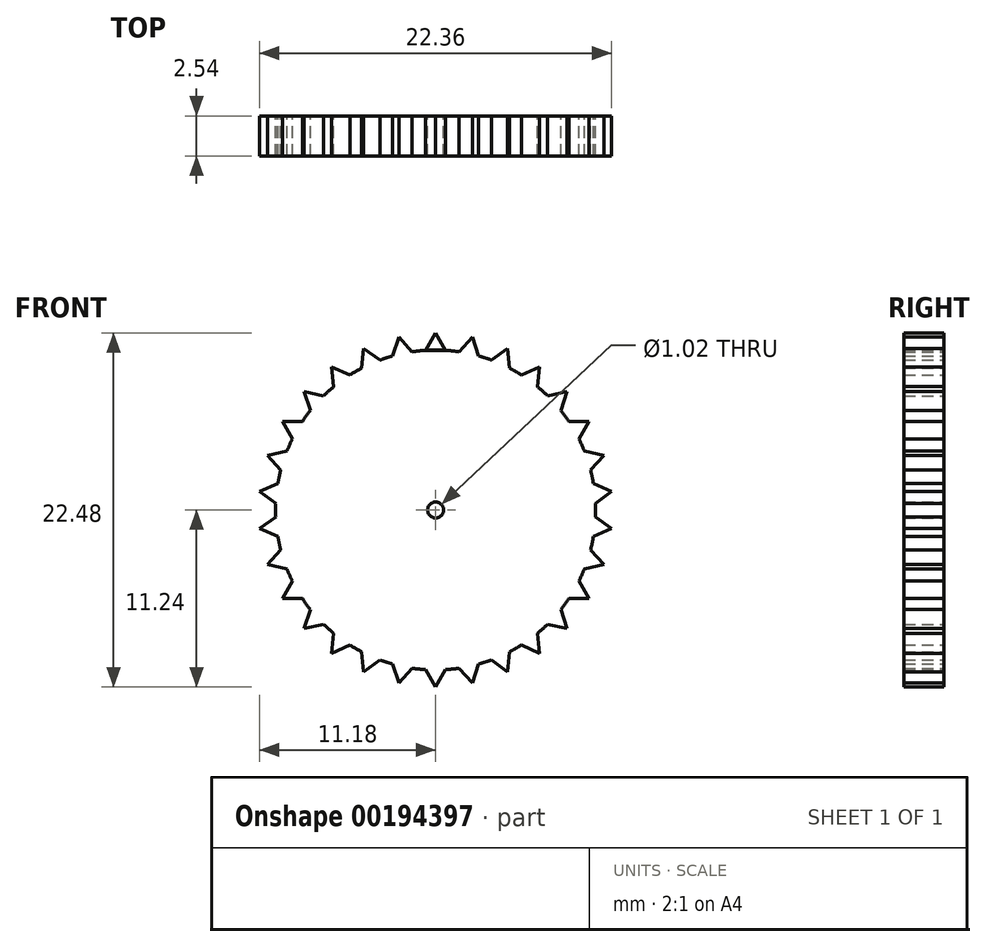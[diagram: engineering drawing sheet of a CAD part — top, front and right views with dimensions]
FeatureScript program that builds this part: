
annotation { "Feature Type Name" : "Feature", "Feature Type Description" : "" }
export const myFeature = defineFeature(function(context is Context, id is Id, definition is map)
    precondition{}
    {
        {
            var Q0;
            Q0=qCreatedBy(makeId("Front.planeOp"),FACE);
            var sketch = newSketch(context, id + "F0", { "sketchPlane" : qUnion([Q0])});
            skCircle(sketch, "E0", {"center": v(0, 0) * mm, "radius": 10.16 * mm});
            skCircle(sketch, "E1", {"center": v(0, 0) * mm, "radius": 0.5 * mm});
            skLineSegment(sketch, "E2", {"start": v(0, 11.24) * mm, "end": v(-0.64, 10.14) * mm});
            skLineSegment(sketch, "E3", {"start": v(-0.64, 10.14) * mm, "end": v(0.64, 10.14) * mm});
            skLineSegment(sketch, "E4", {"start": v(0.64, 10.14) * mm, "end": v(0, 11.24) * mm});
            skLineSegment(sketch, "E5.1.0", {"start": v(-1.49, 10.05) * mm, "end": v(-2.34, 11) * mm});
            skLineSegment(sketch, "E5.1.1", {"start": v(-2.34, 11) * mm, "end": v(-2.73, 9.79) * mm});
            skLineSegment(sketch, "E5.2.0", {"start": v(-3.54, 9.52) * mm, "end": v(-4.57, 10.27) * mm});
            skLineSegment(sketch, "E5.2.1", {"start": v(-4.57, 10.27) * mm, "end": v(-4.7, 9) * mm});
            skLineSegment(sketch, "E5.3.0", {"start": v(-5.45, 8.58) * mm, "end": v(-6.6, 9.1) * mm});
            skLineSegment(sketch, "E5.3.1", {"start": v(-6.6, 9.1) * mm, "end": v(-6.47, 7.83) * mm});
            skLineSegment(sketch, "E5.4.0", {"start": v(-7.11, 7.26) * mm, "end": v(-8.35, 7.52) * mm});
            skLineSegment(sketch, "E5.4.1", {"start": v(-8.35, 7.52) * mm, "end": v(-7.96, 6.31) * mm});
            skLineSegment(sketch, "E5.5.0", {"start": v(-8.46, 5.62) * mm, "end": v(-9.73, 5.62) * mm});
            skLineSegment(sketch, "E5.5.1", {"start": v(-9.73, 5.62) * mm, "end": v(-9.1, 4.52) * mm});
            skLineSegment(sketch, "E5.6.0", {"start": v(-9.45, 3.74) * mm, "end": v(-10.7, 3.47) * mm});
            skLineSegment(sketch, "E5.6.1", {"start": v(-10.7, 3.47) * mm, "end": v(-9.84, 2.53) * mm});
            skLineSegment(sketch, "E5.7.0", {"start": v(-10.02, 1.7) * mm, "end": v(-11.18, 1.17) * mm});
            skLineSegment(sketch, "E5.7.1", {"start": v(-11.18, 1.17) * mm, "end": v(-10.15, 0.43) * mm});
            skLineSegment(sketch, "E5.8.0", {"start": v(-10.15, -0.43) * mm, "end": v(-11.18, -1.17) * mm});
            skLineSegment(sketch, "E5.8.1", {"start": v(-11.18, -1.17) * mm, "end": v(-10.02, -1.7) * mm});
            skLineSegment(sketch, "E5.9.0", {"start": v(-9.84, -2.53) * mm, "end": v(-10.7, -3.47) * mm});
            skLineSegment(sketch, "E5.9.1", {"start": v(-10.7, -3.47) * mm, "end": v(-9.45, -3.74) * mm});
            skLineSegment(sketch, "E5.10.0", {"start": v(-9.1, -4.52) * mm, "end": v(-9.73, -5.62) * mm});
            skLineSegment(sketch, "E5.10.1", {"start": v(-9.73, -5.62) * mm, "end": v(-8.46, -5.62) * mm});
            skLineSegment(sketch, "E5.11.0", {"start": v(-7.96, -6.31) * mm, "end": v(-8.35, -7.52) * mm});
            skLineSegment(sketch, "E5.11.1", {"start": v(-8.35, -7.52) * mm, "end": v(-7.11, -7.26) * mm});
            skLineSegment(sketch, "E5.12.0", {"start": v(-6.47, -7.83) * mm, "end": v(-6.6, -9.1) * mm});
            skLineSegment(sketch, "E5.12.1", {"start": v(-6.6, -9.1) * mm, "end": v(-5.45, -8.58) * mm});
            skLineSegment(sketch, "E5.13.0", {"start": v(-4.7, -9) * mm, "end": v(-4.57, -10.27) * mm});
            skLineSegment(sketch, "E5.13.1", {"start": v(-4.57, -10.27) * mm, "end": v(-3.54, -9.52) * mm});
            skLineSegment(sketch, "E5.14.0", {"start": v(-2.73, -9.79) * mm, "end": v(-2.34, -11) * mm});
            skLineSegment(sketch, "E5.14.1", {"start": v(-2.34, -11) * mm, "end": v(-1.49, -10.05) * mm});
            skLineSegment(sketch, "E5.15.0", {"start": v(-0.64, -10.14) * mm, "end": v(0, -11.24) * mm});
            skLineSegment(sketch, "E5.15.1", {"start": v(0, -11.24) * mm, "end": v(0.64, -10.14) * mm});
            skLineSegment(sketch, "E5.16.0", {"start": v(1.49, -10.05) * mm, "end": v(2.34, -11) * mm});
            skLineSegment(sketch, "E5.16.1", {"start": v(2.34, -11) * mm, "end": v(2.73, -9.79) * mm});
            skLineSegment(sketch, "E5.17.0", {"start": v(3.54, -9.52) * mm, "end": v(4.57, -10.27) * mm});
            skLineSegment(sketch, "E5.17.1", {"start": v(4.57, -10.27) * mm, "end": v(4.7, -9) * mm});
            skLineSegment(sketch, "E5.18.0", {"start": v(5.45, -8.58) * mm, "end": v(6.6, -9.1) * mm});
            skLineSegment(sketch, "E5.18.1", {"start": v(6.6, -9.1) * mm, "end": v(6.47, -7.83) * mm});
            skLineSegment(sketch, "E5.19.0", {"start": v(7.11, -7.26) * mm, "end": v(8.35, -7.52) * mm});
            skLineSegment(sketch, "E5.19.1", {"start": v(8.35, -7.52) * mm, "end": v(7.96, -6.31) * mm});
            skLineSegment(sketch, "E5.20.0", {"start": v(8.46, -5.62) * mm, "end": v(9.73, -5.62) * mm});
            skLineSegment(sketch, "E5.20.1", {"start": v(9.73, -5.62) * mm, "end": v(9.1, -4.52) * mm});
            skLineSegment(sketch, "E5.21.0", {"start": v(9.45, -3.74) * mm, "end": v(10.7, -3.47) * mm});
            skLineSegment(sketch, "E5.21.1", {"start": v(10.7, -3.47) * mm, "end": v(9.84, -2.53) * mm});
            skLineSegment(sketch, "E5.22.0", {"start": v(10.02, -1.7) * mm, "end": v(11.18, -1.17) * mm});
            skLineSegment(sketch, "E5.22.1", {"start": v(11.18, -1.17) * mm, "end": v(10.15, -0.43) * mm});
            skLineSegment(sketch, "E5.23.0", {"start": v(10.15, 0.43) * mm, "end": v(11.18, 1.17) * mm});
            skLineSegment(sketch, "E5.23.1", {"start": v(11.18, 1.17) * mm, "end": v(10.02, 1.7) * mm});
            skLineSegment(sketch, "E5.24.0", {"start": v(9.84, 2.53) * mm, "end": v(10.7, 3.47) * mm});
            skLineSegment(sketch, "E5.24.1", {"start": v(10.7, 3.47) * mm, "end": v(9.45, 3.74) * mm});
            skLineSegment(sketch, "E5.25.0", {"start": v(9.1, 4.52) * mm, "end": v(9.73, 5.62) * mm});
            skLineSegment(sketch, "E5.25.1", {"start": v(9.73, 5.62) * mm, "end": v(8.46, 5.62) * mm});
            skLineSegment(sketch, "E5.26.0", {"start": v(7.96, 6.31) * mm, "end": v(8.35, 7.52) * mm});
            skLineSegment(sketch, "E5.26.1", {"start": v(8.35, 7.52) * mm, "end": v(7.11, 7.26) * mm});
            skLineSegment(sketch, "E5.27.0", {"start": v(6.47, 7.83) * mm, "end": v(6.6, 9.1) * mm});
            skLineSegment(sketch, "E5.27.1", {"start": v(6.6, 9.1) * mm, "end": v(5.45, 8.58) * mm});
            skLineSegment(sketch, "E5.28.0", {"start": v(4.7, 9) * mm, "end": v(4.57, 10.27) * mm});
            skLineSegment(sketch, "E5.28.1", {"start": v(4.57, 10.27) * mm, "end": v(3.54, 9.52) * mm});
            skLineSegment(sketch, "E5.29.0", {"start": v(2.73, 9.79) * mm, "end": v(2.34, 11) * mm});
            skLineSegment(sketch, "E5.29.1", {"start": v(2.34, 11) * mm, "end": v(1.49, 10.05) * mm});
            skSolve(sketch);
        }
        {
            var Q0;
            Q0=makeQuery(id+"F0.imprint","IMPRINT",FACE,{"disambiguationData":[TD([[makeQuery(id+"F0.imprint","IMPRINT",EDGE,{"derivedFrom":sQuery(id+"F0.wireOp",EDGE,"E1")}),-1.0]])]});
            var Q1;
            {var subQ0=sQuery(id+"F0.wireOp",EDGE,"E5.6.0");Q1=makeQuery(id+"F0.imprint","IMPRINT",FACE,{"disambiguationData":[TD([[makeQuery(id+"F0.imprint","IMPRINT",EDGE,{"derivedFrom":subQ0}),1.0]])]});}
            var Q2;
            {var subQ0=sQuery(id+"F0.wireOp",EDGE,"E5.5.0");Q2=makeQuery(id+"F0.imprint","IMPRINT",FACE,{"disambiguationData":[TD([[makeQuery(id+"F0.imprint","IMPRINT",EDGE,{"derivedFrom":subQ0}),1.0]])]});}
            var Q3;
            {var subQ0=sQuery(id+"F0.wireOp",EDGE,"E5.4.0");Q3=makeQuery(id+"F0.imprint","IMPRINT",FACE,{"disambiguationData":[TD([[makeQuery(id+"F0.imprint","IMPRINT",EDGE,{"derivedFrom":subQ0}),1.0]])]});}
            var Q4;
            {var subQ0=sQuery(id+"F0.wireOp",EDGE,"E5.3.0");Q4=makeQuery(id+"F0.imprint","IMPRINT",FACE,{"disambiguationData":[TD([[makeQuery(id+"F0.imprint","IMPRINT",EDGE,{"derivedFrom":subQ0}),1.0]])]});}
            var Q5;
            {var subQ0=sQuery(id+"F0.wireOp",EDGE,"E5.2.0");Q5=makeQuery(id+"F0.imprint","IMPRINT",FACE,{"disambiguationData":[TD([[makeQuery(id+"F0.imprint","IMPRINT",EDGE,{"derivedFrom":subQ0}),1.0]])]});}
            var Q6;
            {var subQ0=sQuery(id+"F0.wireOp",EDGE,"E5.1.0");Q6=makeQuery(id+"F0.imprint","IMPRINT",FACE,{"disambiguationData":[TD([[makeQuery(id+"F0.imprint","IMPRINT",EDGE,{"derivedFrom":subQ0}),1.0]])]});}
            var Q7;
            {var subQ1=sQuery(id+"F0.wireOp",EDGE,"E2");Q7=makeQuery(id+"F0.imprint","IMPRINT",FACE,{"disambiguationData":[TD([[makeQuery(id+"F0.imprint","IMPRINT",EDGE,{"derivedFrom":subQ1}),1.0]])]});}
            var Q8;
            {var subQ0=sQuery(id+"F0.wireOp",EDGE,"E5.29.0");Q8=makeQuery(id+"F0.imprint","IMPRINT",FACE,{"disambiguationData":[TD([[makeQuery(id+"F0.imprint","IMPRINT",EDGE,{"derivedFrom":subQ0}),1.0]])]});}
            var Q9;
            {var subQ0=sQuery(id+"F0.wireOp",EDGE,"E5.28.0");Q9=makeQuery(id+"F0.imprint","IMPRINT",FACE,{"disambiguationData":[TD([[makeQuery(id+"F0.imprint","IMPRINT",EDGE,{"derivedFrom":subQ0}),1.0]])]});}
            var Q10;
            {var subQ0=sQuery(id+"F0.wireOp",EDGE,"E5.27.0");Q10=makeQuery(id+"F0.imprint","IMPRINT",FACE,{"disambiguationData":[TD([[makeQuery(id+"F0.imprint","IMPRINT",EDGE,{"derivedFrom":subQ0}),1.0]])]});}
            var Q11;
            {var subQ0=sQuery(id+"F0.wireOp",EDGE,"E5.26.0");Q11=makeQuery(id+"F0.imprint","IMPRINT",FACE,{"disambiguationData":[TD([[makeQuery(id+"F0.imprint","IMPRINT",EDGE,{"derivedFrom":subQ0}),1.0]])]});}
            var Q12;
            {var subQ0=sQuery(id+"F0.wireOp",EDGE,"E5.25.0");Q12=makeQuery(id+"F0.imprint","IMPRINT",FACE,{"disambiguationData":[TD([[makeQuery(id+"F0.imprint","IMPRINT",EDGE,{"derivedFrom":subQ0}),1.0]])]});}
            var Q13;
            {var subQ0=sQuery(id+"F0.wireOp",EDGE,"E5.24.0");Q13=makeQuery(id+"F0.imprint","IMPRINT",FACE,{"disambiguationData":[TD([[makeQuery(id+"F0.imprint","IMPRINT",EDGE,{"derivedFrom":subQ0}),1.0]])]});}
            var Q14;
            {var subQ0=sQuery(id+"F0.wireOp",EDGE,"E5.23.0");Q14=makeQuery(id+"F0.imprint","IMPRINT",FACE,{"disambiguationData":[TD([[makeQuery(id+"F0.imprint","IMPRINT",EDGE,{"derivedFrom":subQ0}),1.0]])]});}
            var Q15;
            {var subQ0=sQuery(id+"F0.wireOp",EDGE,"E5.22.0");Q15=makeQuery(id+"F0.imprint","IMPRINT",FACE,{"disambiguationData":[TD([[makeQuery(id+"F0.imprint","IMPRINT",EDGE,{"derivedFrom":subQ0}),1.0]])]});}
            var Q16;
            {var subQ0=sQuery(id+"F0.wireOp",EDGE,"E5.21.0");Q16=makeQuery(id+"F0.imprint","IMPRINT",FACE,{"disambiguationData":[TD([[makeQuery(id+"F0.imprint","IMPRINT",EDGE,{"derivedFrom":subQ0}),1.0]])]});}
            var Q17;
            {var subQ0=sQuery(id+"F0.wireOp",EDGE,"E5.20.0");Q17=makeQuery(id+"F0.imprint","IMPRINT",FACE,{"disambiguationData":[TD([[makeQuery(id+"F0.imprint","IMPRINT",EDGE,{"derivedFrom":subQ0}),1.0]])]});}
            var Q18;
            {var subQ0=sQuery(id+"F0.wireOp",EDGE,"E5.19.0");Q18=makeQuery(id+"F0.imprint","IMPRINT",FACE,{"disambiguationData":[TD([[makeQuery(id+"F0.imprint","IMPRINT",EDGE,{"derivedFrom":subQ0}),1.0]])]});}
            var Q19;
            {var subQ0=sQuery(id+"F0.wireOp",EDGE,"E5.18.0");Q19=makeQuery(id+"F0.imprint","IMPRINT",FACE,{"disambiguationData":[TD([[makeQuery(id+"F0.imprint","IMPRINT",EDGE,{"derivedFrom":subQ0}),1.0]])]});}
            var Q20;
            {var subQ0=sQuery(id+"F0.wireOp",EDGE,"E5.17.0");Q20=makeQuery(id+"F0.imprint","IMPRINT",FACE,{"disambiguationData":[TD([[makeQuery(id+"F0.imprint","IMPRINT",EDGE,{"derivedFrom":subQ0}),1.0]])]});}
            var Q21;
            {var subQ0=sQuery(id+"F0.wireOp",EDGE,"E5.16.0");Q21=makeQuery(id+"F0.imprint","IMPRINT",FACE,{"disambiguationData":[TD([[makeQuery(id+"F0.imprint","IMPRINT",EDGE,{"derivedFrom":subQ0}),1.0]])]});}
            var Q22;
            {var subQ0=sQuery(id+"F0.wireOp",EDGE,"E5.15.0");Q22=makeQuery(id+"F0.imprint","IMPRINT",FACE,{"disambiguationData":[TD([[makeQuery(id+"F0.imprint","IMPRINT",EDGE,{"derivedFrom":subQ0}),1.0]])]});}
            var Q23;
            {var subQ0=sQuery(id+"F0.wireOp",EDGE,"E5.14.0");Q23=makeQuery(id+"F0.imprint","IMPRINT",FACE,{"disambiguationData":[TD([[makeQuery(id+"F0.imprint","IMPRINT",EDGE,{"derivedFrom":subQ0}),1.0]])]});}
            var Q24;
            {var subQ0=sQuery(id+"F0.wireOp",EDGE,"E5.13.0");Q24=makeQuery(id+"F0.imprint","IMPRINT",FACE,{"disambiguationData":[TD([[makeQuery(id+"F0.imprint","IMPRINT",EDGE,{"derivedFrom":subQ0}),1.0]])]});}
            var Q25;
            {var subQ0=sQuery(id+"F0.wireOp",EDGE,"E5.12.0");Q25=makeQuery(id+"F0.imprint","IMPRINT",FACE,{"disambiguationData":[TD([[makeQuery(id+"F0.imprint","IMPRINT",EDGE,{"derivedFrom":subQ0}),1.0]])]});}
            var Q26;
            {var subQ0=sQuery(id+"F0.wireOp",EDGE,"E5.11.0");Q26=makeQuery(id+"F0.imprint","IMPRINT",FACE,{"disambiguationData":[TD([[makeQuery(id+"F0.imprint","IMPRINT",EDGE,{"derivedFrom":subQ0}),1.0]])]});}
            var Q27;
            {var subQ0=sQuery(id+"F0.wireOp",EDGE,"E5.10.0");Q27=makeQuery(id+"F0.imprint","IMPRINT",FACE,{"disambiguationData":[TD([[makeQuery(id+"F0.imprint","IMPRINT",EDGE,{"derivedFrom":subQ0}),1.0]])]});}
            var Q28;
            {var subQ0=sQuery(id+"F0.wireOp",EDGE,"E5.9.0");Q28=makeQuery(id+"F0.imprint","IMPRINT",FACE,{"disambiguationData":[TD([[makeQuery(id+"F0.imprint","IMPRINT",EDGE,{"derivedFrom":subQ0}),1.0]])]});}
            var Q29;
            {var subQ0=sQuery(id+"F0.wireOp",EDGE,"E5.8.0");Q29=makeQuery(id+"F0.imprint","IMPRINT",FACE,{"disambiguationData":[TD([[makeQuery(id+"F0.imprint","IMPRINT",EDGE,{"derivedFrom":subQ0}),1.0]])]});}
            var Q30;
            {var subQ0=sQuery(id+"F0.wireOp",EDGE,"E5.7.0");Q30=makeQuery(id+"F0.imprint","IMPRINT",FACE,{"disambiguationData":[TD([[makeQuery(id+"F0.imprint","IMPRINT",EDGE,{"derivedFrom":subQ0}),1.0]])]});}
            extrude(context, id + "F1", {"entities" : qUnion([Q0, Q1, Q2, Q3, Q4, Q5, Q6, Q7, Q8, Q9, Q10, Q11, Q12, Q13, Q14, Q15, Q16, Q17, Q18, Q19, Q20, Q21, Q22, Q23, Q24, Q25, Q26, Q27, Q28, Q29, Q30]), "depth" : 2.54 * mm});
        }
    });
